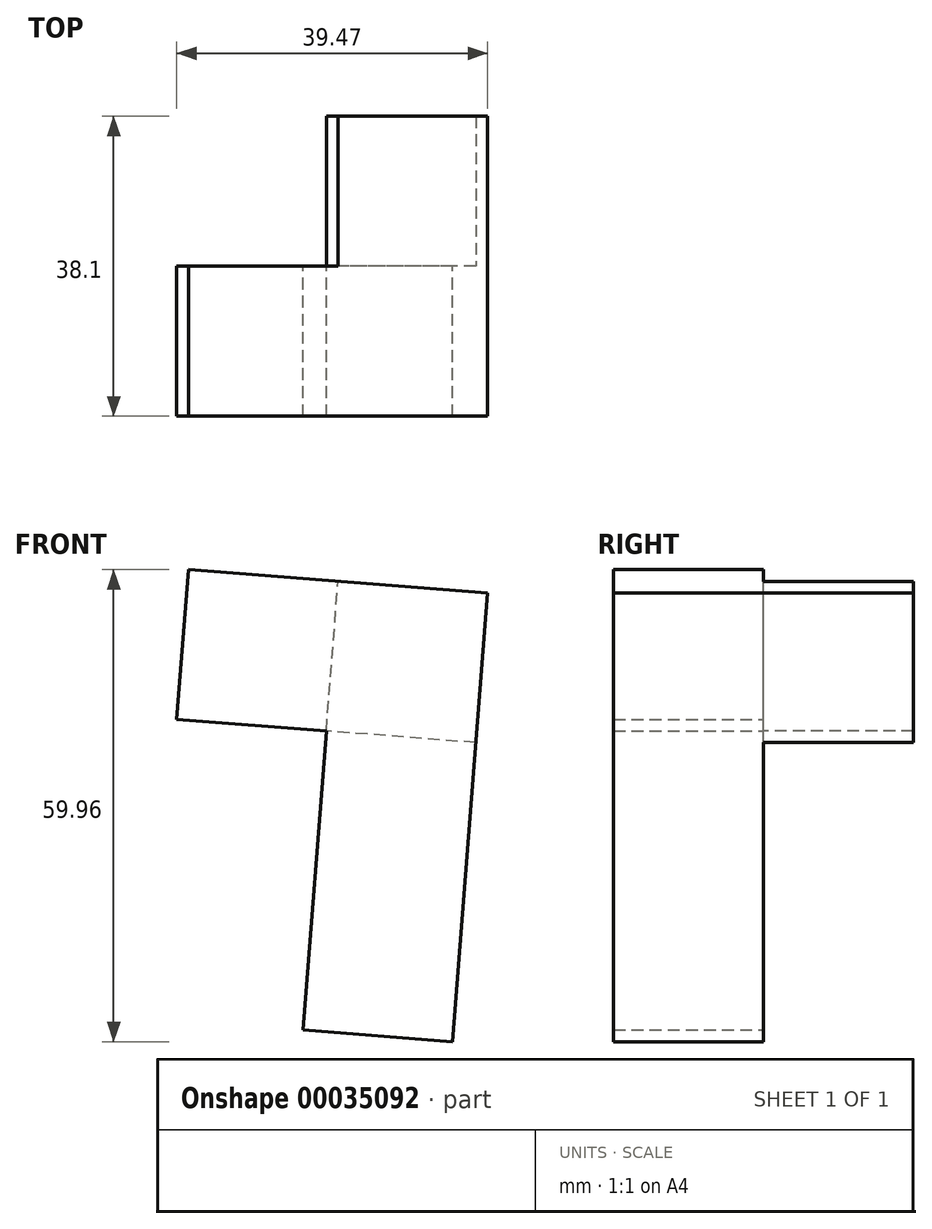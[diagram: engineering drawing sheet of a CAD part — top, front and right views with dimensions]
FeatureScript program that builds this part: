
annotation { "Feature Type Name" : "Feature", "Feature Type Description" : "" }
export const myFeature = defineFeature(function(context is Context, id is Id, definition is map)
    precondition{}
    {
        {
            var Q0;
            Q0=qCreatedBy(makeId("Front.planeOp"),FACE);
            var sketch = newSketch(context, id + "F0", { "sketchPlane" : qUnion([Q0])});
            skLineSegment(sketch, "E0", {"start": v(9.66, 33.24) * mm, "end": v(47.64, 30.26) * mm});
            skLineSegment(sketch, "E1", {"start": v(47.64, 30.26) * mm, "end": v(43.18, -26.72) * mm});
            skLineSegment(sketch, "E2", {"start": v(43.18, -26.72) * mm, "end": v(24.19, -25.23) * mm});
            skLineSegment(sketch, "E3", {"start": v(24.19, -25.23) * mm, "end": v(27.16, 12.76) * mm});
            skLineSegment(sketch, "E4", {"start": v(27.16, 12.76) * mm, "end": v(8.17, 14.24) * mm});
            skLineSegment(sketch, "E5", {"start": v(8.17, 14.24) * mm, "end": v(9.66, 33.24) * mm});
            skSolve(sketch);
        }
        {
            var Q0;
            Q0 = qSketchRegion(id + "F0", true);
            extrude(context, id + "F1", {"entities" : qUnion([Q0]), "depth" : 19.05 * mm});
        }
        {
            var Q0;
            Q0=makeQuery(id+"F0.imprint","IMPRINT",FACE,{"disambiguationData":[TD([[makeQuery(id+"F0.imprint","IMPRINT",EDGE,{"derivedFrom":sQuery(id+"F0.wireOp",EDGE,"E0")}),-1.0]])]});
            var sketch = newSketch(context, id + "F2", { "sketchPlane" : qUnion([Q0])});
            skPoint(sketch, "E6.0", {"position": v(47.64, 30.26) * mm});
            skLineSegment(sketch, "E7.0", {"start": v(47.64, 30.26) * mm, "end": v(43.18, -26.72) * mm});
            skLineSegment(sketch, "E8", {"start": v(47.64, 30.26) * mm, "end": v(46.15, 11.27) * mm});
            skLineSegment(sketch, "E9", {"start": v(46.15, 11.27) * mm, "end": v(27.16, 12.76) * mm});
            skLineSegment(sketch, "E10", {"start": v(27.16, 12.76) * mm, "end": v(28.65, 31.75) * mm});
            skLineSegment(sketch, "E11", {"start": v(28.65, 31.75) * mm, "end": v(47.64, 30.26) * mm});
            skSolve(sketch);
        }
        {
            var Q0;
            Q0 = qSketchRegion(id + "F2", true);
            extrude(context, id + "F3", {"entities" : qUnion([Q0]), "operationType" : NewBodyOperationType.ADD, "oppositeDirection" : true, "depth" : 19.05 * mm});
        }
    });
